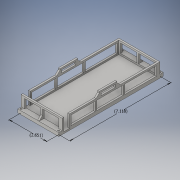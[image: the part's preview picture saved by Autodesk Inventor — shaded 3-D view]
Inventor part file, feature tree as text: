
AUTODESK INVENTOR PART (.ipt)
format: ipt  version: 2016 (Build 200138000, 138)  size: 279,040 bytes
history: native  units: in
note: dims shown in document units (in); Inventor stores cm internally (conversion verified against a paired STEP export)
features: sketch x9, extrude x8, chamfer x1
ambient origin geometry x8: Origin, YZ Plane, XZ Plane, XY Plane, X Axis, Y Axis, Z Axis, Center Point
bodies: Solid1 (feature_tree)
feature tree (18):
  extrude  "Extrusion1"  Depth=2.647in
  extrude  "Extrusion2"  Depth=0.12in
  extrude  "Extrusion3"  Depth=0.12in
  extrude  "Extrusion4"  Depth=0.12in
  extrude  "Extrusion5"  Depth=0.4in
  extrude  "Extrusion6"  Depth=0.24in
  extrude  "Extrusion7"  Depth=0.24in
  extrude  "Extrusion8"  Depth=0.12in
  chamfer  "Chamfer1"  Distance=15.7in
  sketch  "Sketch9"  dims[d24=0.06in d25=15.7in d26=0.0in d27=0.24in d28=0.12in d29=0.24in d30=0.12in d31=0.12in d32=0.12in d33=15.7in d34=0.0in d35=0.1181in d36=0.1181in d37=0.1181in d38=0.1181in d39=0.1181in d40=0.118in d41=0.118in d42=0.1181in d43=0.118in d44=0.0in d45=0.1181in d46=0.0in d47=0.1181in d48=0.1181in d49=0.24in d50=0.0in d51=1.0in d52=0.2in d53=0.12in d54=0.12in d55=0.12in d56=2.887in d57=0.0in d58=0.4in d59=0.0in d60=0.23in d61=0.125in d62=45.0deg d63=7.1181in d64=2.6509in]
  sketch  "Sketch1"  dims[d0=6.642in d1=2.647in]
  sketch  "Sketch2"  dims[d2=0.12in d3=0.12in]
  sketch  "Sketch3"  dims[d4=0.12in d5=0.12in]
  sketch  "Sketch4"  dims[d6=1.0in d7=0.0in d8=0.12in]
  sketch  "Sketch5"  dims[d9=2.7in d10=0.0in d11=0.4in]
  sketch  "Sketch6"  dims[d12=5.7in d13=0.0in d14=0.24in]
  sketch  "Sketch7"  dims[d15=0.24in d16=0.24in]
  sketch  "Sketch8"  dims[d17=0.12in d23=0.06in]
